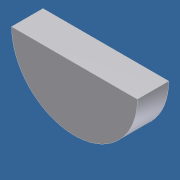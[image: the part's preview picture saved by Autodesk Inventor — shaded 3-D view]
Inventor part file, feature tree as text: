
AUTODESK INVENTOR PART (.ipt)
format: ipt  version: unknown  size: 142,140 bytes
history: native  units: mm (DEFAULTED — no unit token found)
features: extrude x1, sketch x1
ambient origin geometry x8: Origin, YZ Plane, XZ Plane, XY Plane, X Axis, Y Axis, Z Axis, Center Point
bodies: Solid1 (feature_tree)
feature tree (2):
  extrude  "Extrusion1"  Depth=3.175mm TaperAngle=0.0deg
  sketch  "Sketch1"  dims[d0=12.7mm d1=3.175mm d2=0.0mm]
